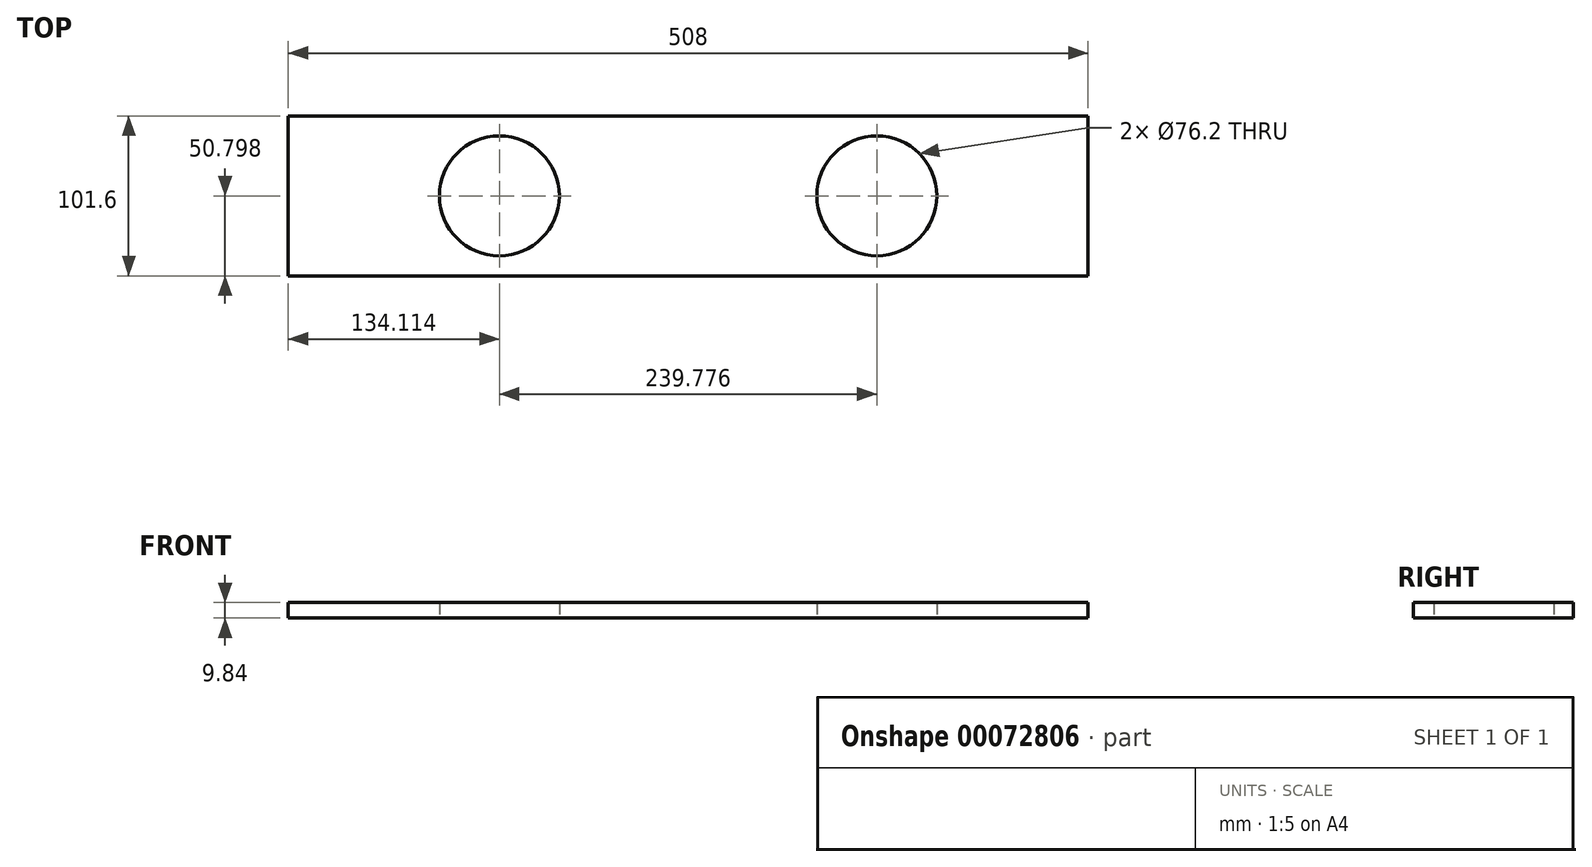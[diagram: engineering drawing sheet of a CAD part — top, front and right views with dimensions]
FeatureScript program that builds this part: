
annotation { "Feature Type Name" : "Feature", "Feature Type Description" : "" }
export const myFeature = defineFeature(function(context is Context, id is Id, definition is map)
    precondition{}
    {
        {
            var Q0;
            Q0=qCreatedBy(makeId("Top.planeOp"),FACE);
            var sketch = newSketch(context, id + "F0", { "sketchPlane" : qUnion([Q0])});
            skLineSegment(sketch, "E0.bottom", {"start": v(-248.46, 33.86) * mm, "end": v(259.54, 33.86) * mm});
            skLineSegment(sketch, "E0.top", {"start": v(-248.46, -67.74) * mm, "end": v(259.54, -67.74) * mm});
            skLineSegment(sketch, "E0.left", {"start": v(-248.46, 33.86) * mm, "end": v(-248.46, -67.74) * mm});
            skLineSegment(sketch, "E0.right", {"start": v(259.54, 33.86) * mm, "end": v(259.54, -67.74) * mm});
            skCircle(sketch, "E1", {"center": v(-114.35, -16.94) * mm, "radius": 38.1 * mm});
            skPoint(sketch, "E1.centerSnap0", {"position": v(-248.46, -16.94) * mm});
            skCircle(sketch, "E2", {"center": v(125.43, -16.94) * mm, "radius": 38.1 * mm});
            skSolve(sketch);
        }
        {
            var Q0;
            Q0=makeQuery(id+"F0.imprint","IMPRINT",FACE,{"disambiguationData":[TD([[makeQuery(id+"F0.imprint","IMPRINT",EDGE,{"derivedFrom":sQuery(id+"F0.wireOp",EDGE,"E0.bottom")}),-1.0]])]});
            extrude(context, id + "F1", {"entities" : qUnion([Q0]), "depth" : 9.84 * mm});
        }
    });
